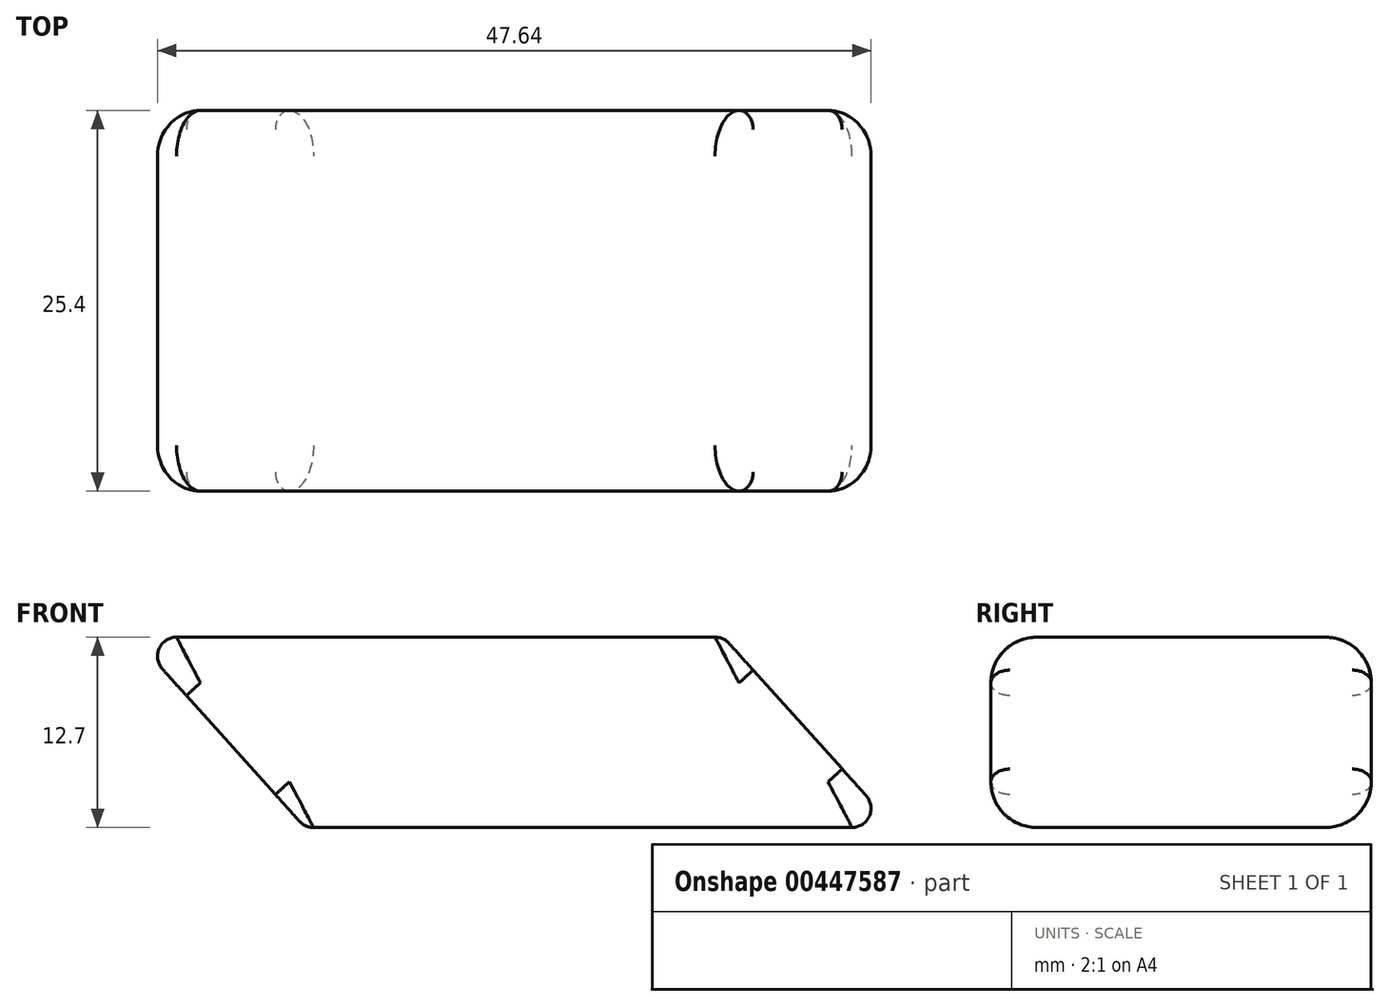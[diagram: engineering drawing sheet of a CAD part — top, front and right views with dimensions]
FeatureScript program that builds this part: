
annotation { "Feature Type Name" : "Feature", "Feature Type Description" : "" }
export const myFeature = defineFeature(function(context is Context, id is Id, definition is map)
    precondition{}
    {
        {
            var Q0;
            Q0=qCreatedBy(makeId("Front.planeOp"),FACE);
            var sketch = newSketch(context, id + "F0", { "sketchPlane" : qUnion([Q0])});
            skLineSegment(sketch, "E0.bottom", {"start": v(0, 0) * mm, "end": v(50.8, 0) * mm});
            skLineSegment(sketch, "E0.top", {"start": v(0, -12.7) * mm, "end": v(50.8, -12.7) * mm});
            skLineSegment(sketch, "E0.left", {"start": v(0, 0) * mm, "end": v(0, -12.7) * mm});
            skLineSegment(sketch, "E0.right", {"start": v(50.8, 0) * mm, "end": v(50.8, -12.7) * mm});
            skLineSegment(sketch, "E1", {"start": v(50.8, -12.7) * mm, "end": v(39.37, 0) * mm});
            skLineSegment(sketch, "E2", {"start": v(0, 0) * mm, "end": v(11.43, -12.7) * mm});
            skSolve(sketch);
        }
        {
            var Q0;
            {var subQ2=sQuery(id+"F0.wireOp",EDGE,"E1");Q0=makeQuery(id+"F0.imprint","IMPRINT",FACE,{"disambiguationData":[TD([[makeQuery(id+"F0.imprint","IMPRINT",EDGE,{"derivedFrom":subQ2}),1.0]])]});}
            extrude(context, id + "F1", {"entities" : qUnion([Q0]), "depth" : 25.4 * mm});
        }
        {
            var Q0;
            Q0=makeQuery(id+"F1.opExtrude","CAP_EDGE",EDGE,{"disambiguationData":[OSD([sQuery(id+"F0.wireOp",EDGE,"E0.top")])],"isStart":false});
            var Q1;
            Q1=makeQuery(id+"F1.opExtrude","CAP_EDGE",EDGE,{"disambiguationData":[OSD([sQuery(id+"F0.wireOp",EDGE,"E0.bottom")])],"isStart":false});
            var Q2;
            Q2=makeQuery(id+"F1.opExtrude","CAP_EDGE",EDGE,{"disambiguationData":[OSD([sQuery(id+"F0.wireOp",EDGE,"E0.top")])],"isStart":true});
            var Q3;
            Q3=makeQuery(id+"F1.opExtrude","CAP_EDGE",EDGE,{"disambiguationData":[OSD([sQuery(id+"F0.wireOp",EDGE,"E0.bottom")])],"isStart":true});
            fillet(context, id + "F2", {"entities" : qUnion([Q0, Q1, Q2, Q3]), "radius" : 3.05 * mm, "tangentPropagation" : true, "allowEdgeOverflow" : false});
        }
        {
            var Q0;
            Q0=makeQuery(id+"F1.opExtrude","SWEPT_EDGE",EDGE,{"disambiguationData":[OSD([sQuery(id+"F0.wireOp",EDGE,"E0.bottom"),sQuery(id+"F0.wireOp",EDGE,"E0.left"),sQuery(id+"F0.wireOp",EDGE,"E2")])]});
            var Q1;
            Q1=makeQuery(id+"F1.opExtrude","SWEPT_EDGE",EDGE,{"disambiguationData":[OSD([sQuery(id+"F0.wireOp",EDGE,"E0.top"),sQuery(id+"F0.wireOp",EDGE,"E0.right"),sQuery(id+"F0.wireOp",EDGE,"E1")])]});
            var Q2;
            Q2=makeQuery(id+"F1.opExtrude","SWEPT_EDGE",EDGE,{"disambiguationData":[OSD([sQuery(id+"F0.wireOp",EDGE,"E0.bottom"),sQuery(id+"F0.wireOp",EDGE,"E1")])]});
            var Q3;
            Q3=makeQuery(id+"F1.opExtrude","SWEPT_EDGE",EDGE,{"disambiguationData":[OSD([sQuery(id+"F0.wireOp",EDGE,"E0.top"),sQuery(id+"F0.wireOp",EDGE,"E2")])]});
            fillet(context, id + "F3", {"entities" : qUnion([Q0, Q1, Q2, Q3]), "radius" : 1.27 * mm, "tangentPropagation" : true, "allowEdgeOverflow" : false});
        }
    });
